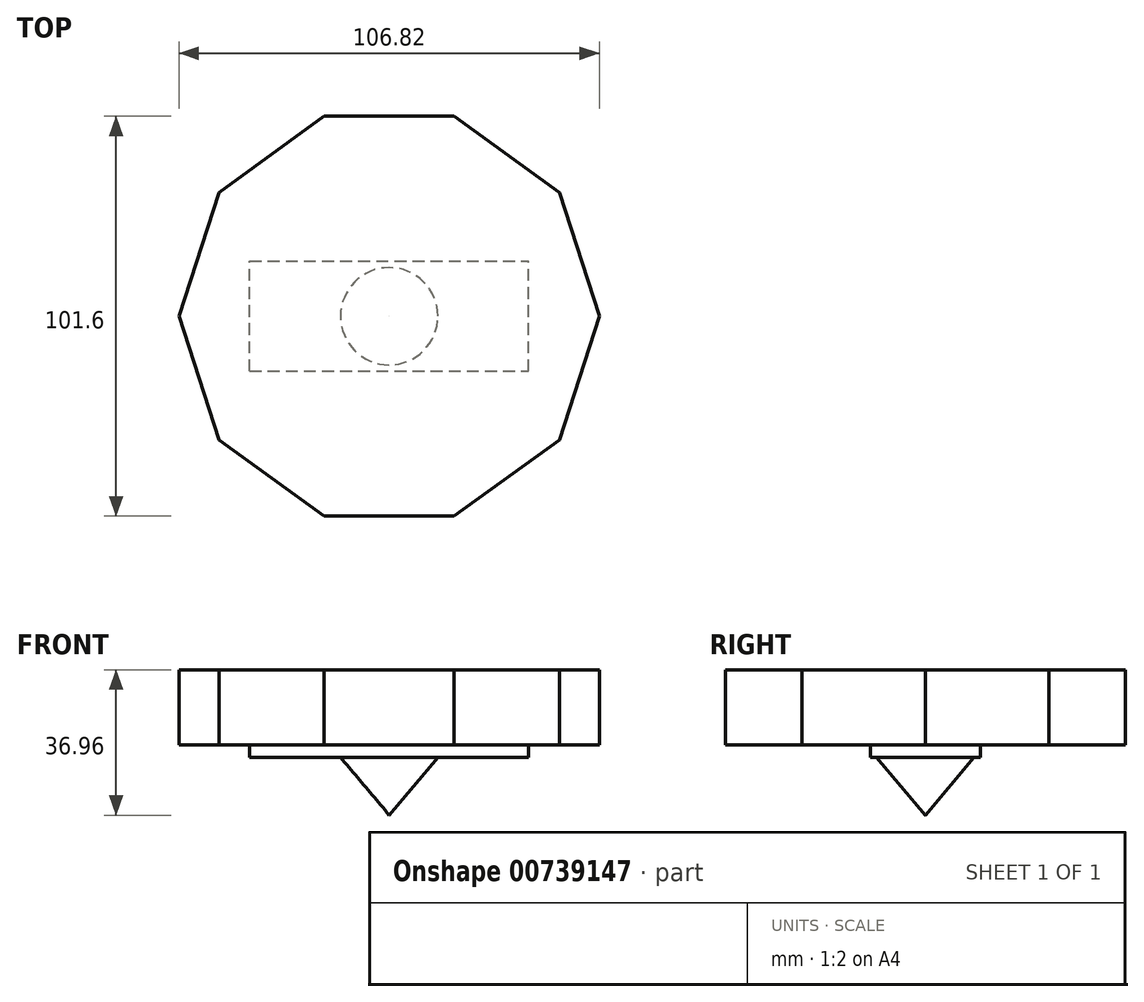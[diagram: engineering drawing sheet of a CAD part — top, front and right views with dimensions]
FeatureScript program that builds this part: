
annotation { "Feature Type Name" : "Feature", "Feature Type Description" : "" }
export const myFeature = defineFeature(function(context is Context, id is Id, definition is map)
    precondition{}
    {
        {
            var Q0;
            Q0=qCreatedBy(makeId("Top.planeOp"),FACE);
            var sketch = newSketch(context, id + "F0", { "sketchPlane" : qUnion([Q0])});
            skCircle(sketch, "E0.cCircle", {"center": v(0, 0) * mm, "radius": 50.8 * mm, "construction": true});
            skLineSegment(sketch, "E0.0", {"start": v(16.5, -50.8) * mm, "end": v(-16.5, -50.8) * mm});
            skLineSegment(sketch, "E0.1", {"start": v(-16.5, -50.8) * mm, "end": v(-43.21, -31.4) * mm});
            skLineSegment(sketch, "E0.2", {"start": v(-43.21, -31.4) * mm, "end": v(-53.41, 0) * mm});
            skLineSegment(sketch, "E0.3", {"start": v(-53.41, 0) * mm, "end": v(-43.21, 31.4) * mm});
            skLineSegment(sketch, "E0.4", {"start": v(-43.21, 31.4) * mm, "end": v(-16.5, 50.8) * mm});
            skLineSegment(sketch, "E0.5", {"start": v(-16.5, 50.8) * mm, "end": v(16.5, 50.8) * mm});
            skLineSegment(sketch, "E0.6", {"start": v(16.5, 50.8) * mm, "end": v(43.21, 31.4) * mm});
            skLineSegment(sketch, "E0.7", {"start": v(43.21, 31.4) * mm, "end": v(53.41, 0) * mm});
            skLineSegment(sketch, "E0.8", {"start": v(53.41, 0) * mm, "end": v(43.21, -31.4) * mm});
            skLineSegment(sketch, "E0.9", {"start": v(43.21, -31.4) * mm, "end": v(16.5, -50.8) * mm});
            skPoint(sketch, "E0.0.midPoint", {"position": v(0, -50.8) * mm});
            skSolve(sketch);
        }
        {
            var Q0;
            Q0 = qSketchRegion(id + "F0", true);
            extrude(context, id + "F1", {"entities" : qUnion([Q0]), "depth" : 19.05 * mm, "offsetDistance" : 25.4 * mm});
        }
        {
            var Q0;
            Q0=makeQuery(id+"F1.opExtrude","CAP_FACE",FACE,{"disambiguationData":[OSD([sQuery(id+"F0.wireOp",EDGE,"E0.0"),sQuery(id+"F0.wireOp",EDGE,"E0.1"),sQuery(id+"F0.wireOp",EDGE,"E0.2"),sQuery(id+"F0.wireOp",EDGE,"E0.3"),sQuery(id+"F0.wireOp",EDGE,"E0.4"),sQuery(id+"F0.wireOp",EDGE,"E0.5"),sQuery(id+"F0.wireOp",EDGE,"E0.6"),sQuery(id+"F0.wireOp",EDGE,"E0.7"),sQuery(id+"F0.wireOp",EDGE,"E0.8"),sQuery(id+"F0.wireOp",EDGE,"E0.9")])],"isStart":true});
            var sketch = newSketch(context, id + "F2", { "sketchPlane" : qUnion([Q0])});
            skLineSegment(sketch, "E1.bottom", {"start": v(-35.44, 13.97) * mm, "end": v(35.44, 13.97) * mm});
            skLineSegment(sketch, "E1.top", {"start": v(-35.44, -13.97) * mm, "end": v(35.44, -13.97) * mm});
            skLineSegment(sketch, "E1.left", {"start": v(-35.44, 13.97) * mm, "end": v(-35.44, -13.97) * mm});
            skLineSegment(sketch, "E1.right", {"start": v(35.44, 13.97) * mm, "end": v(35.44, -13.97) * mm});
            skPoint(sketch, "E2", {"position": v(0, 13.97) * mm});
            skPoint(sketch, "E3", {"position": v(-35.44, 0) * mm});
            skSolve(sketch);
        }
        {
            var Q0;
            Q0 = qSketchRegion(id + "F2", true);
            extrude(context, id + "F3", {"entities" : qUnion([Q0]), "operationType" : NewBodyOperationType.ADD, "depth" : 3.17 * mm, "offsetDistance" : 25.4 * mm});
        }
        {
            var Q0;
            Q0=makeQuery(id+"F3.opExtrude","CAP_FACE",FACE,{"disambiguationData":[OSD([sQuery(id+"F2.wireOp",EDGE,"E1.bottom"),sQuery(id+"F2.wireOp",EDGE,"E1.top"),sQuery(id+"F2.wireOp",EDGE,"E1.left"),sQuery(id+"F2.wireOp",EDGE,"E1.right")])],"isStart":false});
            var sketch = newSketch(context, id + "F4", { "sketchPlane" : qUnion([Q0])});
            skCircle(sketch, "E4", {"center": v(0, 0) * mm, "radius": 12.69 * mm});
            skSolve(sketch);
        }
        {
            var Q0;
            Q0 = qSketchRegion(id + "F4", true);
            extrude(context, id + "F5", {"entities" : qUnion([Q0]), "operationType" : NewBodyOperationType.ADD, "depth" : 14.73 * mm, "offsetDistance" : 25.4 * mm});
        }
        {
            var Q0;
            Q0=makeQuery(id+"F5.opExtrude","CAP_EDGE",EDGE,{"disambiguationData":[OSD([sQuery(id+"F4.wireOp",EDGE,"E4")])],"isStart":false});
            chamfer(context, id + "F6", {"entities" : qUnion([Q0]), "chamferType" : ChamferType.OFFSET_ANGLE, "width" : 12.7 * mm, "oppositeDirection" : false, "angle" : 50 * degree, "tangentPropagation" : true});
        }
    });
